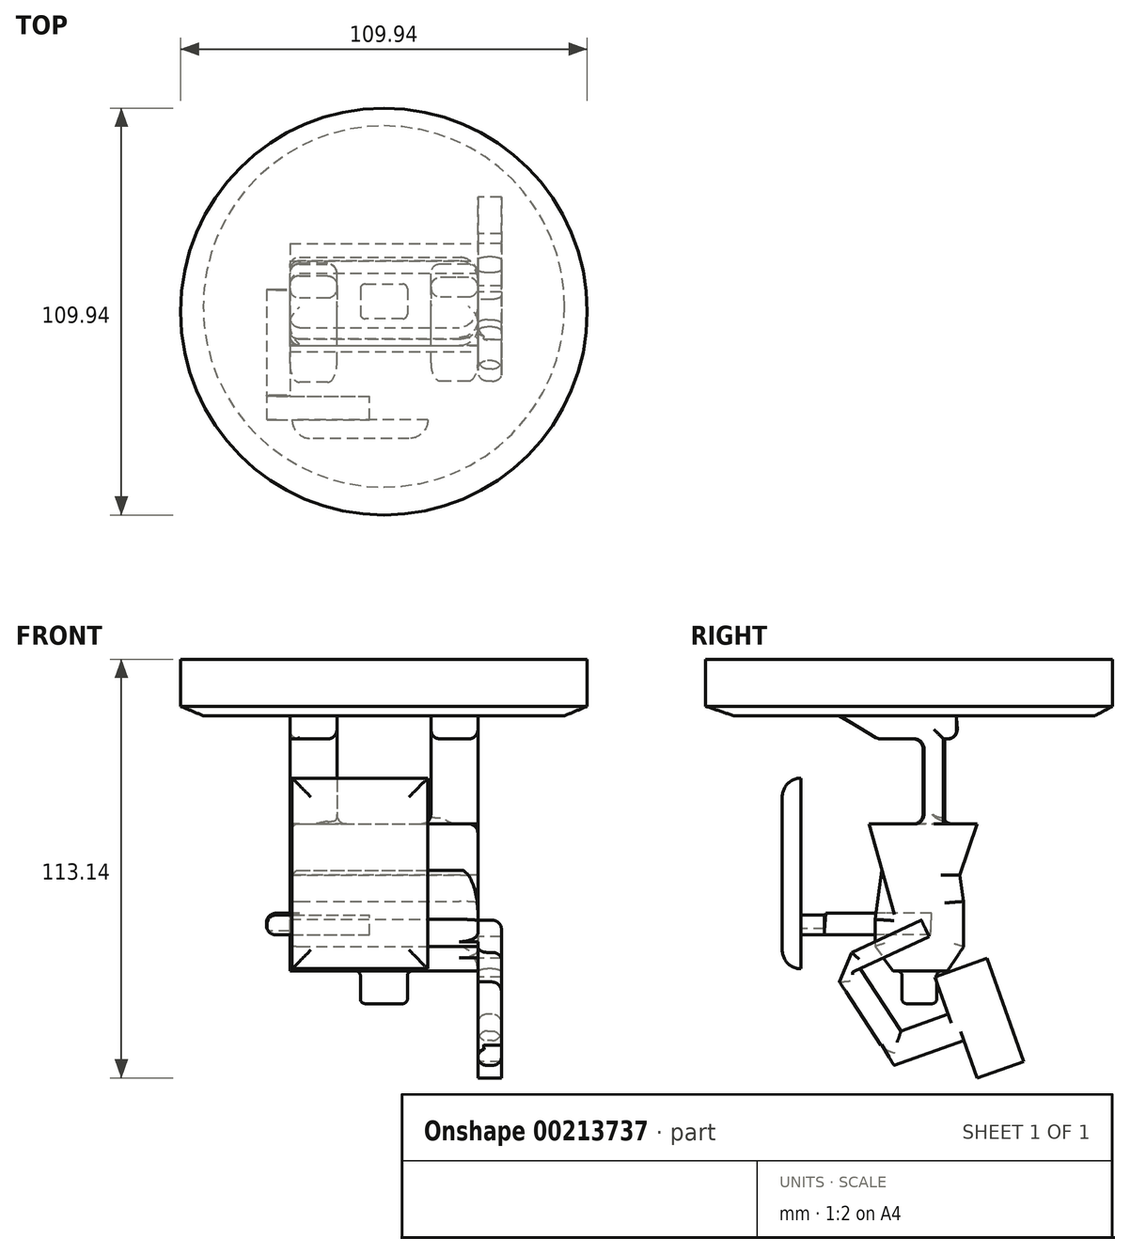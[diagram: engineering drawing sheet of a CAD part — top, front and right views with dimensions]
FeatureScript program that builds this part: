
annotation { "Feature Type Name" : "Feature", "Feature Type Description" : "" }
export const myFeature = defineFeature(function(context is Context, id is Id, definition is map)
    precondition{}
    {
        {
            var Q0;
            Q0=qCreatedBy(makeId("Top.planeOp"),FACE);
            var sketch = newSketch(context, id + "F0", { "sketchPlane" : qUnion([Q0])});
            skCircle(sketch, "E0", {"center": v(0, 0) * mm, "radius": 54.97 * mm});
            skSolve(sketch);
        }
        {
            var Q0;
            Q0 = qSketchRegion(id + "F0", true);
            var Q1;
            Q1=sQuery(id+"F0.wireOp",EDGE,"E0");
            extrude(context, id + "F1", {"entities" : qUnion([Q0]), "surfaceEntities" : qUnion([Q1]), "depth" : 12.7 * mm});
        }
        {
            var Q0;
            Q0=qCreatedBy(makeId("Top.planeOp"),FACE);
            cPlane(context, id + "F2", {"entities" : qUnion([Q0]), "cplaneType" : CPlaneType.OFFSET, "offset" : 2.54 * mm, "oppositeDirection" : true, "width" : 152.4 * mm, "height" : 152.4 * mm});
        }
        {
            var Q0;
            Q0=qCreatedBy(id+"F2.planeOp",FACE);
            var sketch = newSketch(context, id + "F3", { "sketchPlane" : qUnion([Q0])});
            skCircle(sketch, "E1", {"center": v(0, 1.38) * mm, "radius": 48.83 * mm});
            skSolve(sketch);
        }
        {
            var Q0;
            Q0 = qSketchRegion(id + "F3", true);
            var Q1;
            Q1 = qSketchRegion(id + "F0", true);
            loft(context, id + "F4", {"sheetProfilesArray" : [{ "sheetProfileEntities" : qUnion([Q0]) }, { "sheetProfileEntities" : qUnion([Q1]) }]});
        }
        {
            var Q0;
            Q0=qCreatedBy(makeId("Right.planeOp"),FACE);
            cPlane(context, id + "F5", {"entities" : qUnion([Q0]), "cplaneType" : CPlaneType.OFFSET, "offset" : 25.4 * mm, "width" : 152.4 * mm, "height" : 152.4 * mm});
        }
        {
            var Q0;
            Q0=qCreatedBy(makeId("Right.planeOp"),FACE);
            cPlane(context, id + "F6", {"entities" : qUnion([Q0]), "cplaneType" : CPlaneType.OFFSET, "offset" : 25.4 * mm, "oppositeDirection" : true, "width" : 152.4 * mm, "height" : 152.4 * mm});
        }
        {
            var Q0;
            Q0=qCreatedBy(id+"F6.planeOp",FACE);
            var sketch = newSketch(context, id + "F7", { "sketchPlane" : qUnion([Q0])});
            skLineSegment(sketch, "E2", {"start": v(-19.43, -2.33) * mm, "end": v(-8.14, -8.84) * mm});
            skLineSegment(sketch, "E3", {"start": v(-8.14, -8.84) * mm, "end": v(0, -8.84) * mm});
            skLineSegment(sketch, "E4", {"start": v(0, -8.84) * mm, "end": v(6.5, -8.84) * mm});
            skLineSegment(sketch, "E5", {"start": v(6.5, -8.84) * mm, "end": v(13.13, -8.84) * mm});
            skLineSegment(sketch, "E6", {"start": v(13.13, -8.84) * mm, "end": v(12.81, -2.19) * mm});
            skLineSegment(sketch, "E7", {"start": v(12.81, -2.19) * mm, "end": v(-19.43, -2.33) * mm});
            skSolve(sketch);
        }
        {
            var Q0;
            Q0 = qSketchRegion(id + "F7", true);
            extrude(context, id + "F8", {"entities" : qUnion([Q0]), "operationType" : NewBodyOperationType.ADD, "depth" : 12.7 * mm});
        }
        {
            var Q0;
            Q0=qCreatedBy(id+"F5.planeOp",FACE);
            var sketch = newSketch(context, id + "F9", { "sketchPlane" : qUnion([Q0])});
            skLineSegment(sketch, "E8", {"start": v(-19.1, -2.33) * mm, "end": v(-8.3, -8.84) * mm});
            skLineSegment(sketch, "E9", {"start": v(-8.3, -8.84) * mm, "end": v(12.85, -8.84) * mm});
            skLineSegment(sketch, "E10", {"start": v(12.85, -8.84) * mm, "end": v(12.85, -2.33) * mm});
            skLineSegment(sketch, "E11", {"start": v(12.85, -2.33) * mm, "end": v(-19.1, -2.33) * mm});
            skSolve(sketch);
        }
        {
            var Q0;
            Q0 = qSketchRegion(id + "F9", true);
            extrude(context, id + "F10", {"entities" : qUnion([Q0]), "operationType" : NewBodyOperationType.ADD, "oppositeDirection" : true, "depth" : 12.7 * mm});
        }
        {
            var Q0;
            Q0=qCreatedBy(id+"F6.planeOp",FACE);
            var sketch = newSketch(context, id + "F11", { "sketchPlane" : qUnion([Q0])});
            skLineSegment(sketch, "E12", {"start": v(9.67, -8.53) * mm, "end": v(9.67, -32.5) * mm});
            skLineSegment(sketch, "E13", {"start": v(3.73, -8.4) * mm, "end": v(3.73, -32.5) * mm});
            skLineSegment(sketch, "E14", {"start": v(3.73, -32.5) * mm, "end": v(9.67, -32.5) * mm});
            skLineSegment(sketch, "E15", {"start": v(9.67, -8.53) * mm, "end": v(3.73, -8.4) * mm});
            skSolve(sketch);
        }
        {
            var Q0;
            Q0 = qSketchRegion(id + "F11", true);
            extrude(context, id + "F12", {"entities" : qUnion([Q0]), "operationType" : NewBodyOperationType.ADD, "depth" : 12.7 * mm});
        }
        {
            var Q0;
            Q0=qCreatedBy(id+"F5.planeOp",FACE);
            var sketch = newSketch(context, id + "F13", { "sketchPlane" : qUnion([Q0])});
            skLineSegment(sketch, "E16", {"start": v(9.26, -8.56) * mm, "end": v(9.26, -33.06) * mm});
            skLineSegment(sketch, "E17", {"start": v(9.26, -33.06) * mm, "end": v(4, -33.06) * mm});
            skLineSegment(sketch, "E18", {"start": v(4, -33.06) * mm, "end": v(4, -8.28) * mm});
            skLineSegment(sketch, "E19", {"start": v(4, -8.28) * mm, "end": v(9.26, -8.56) * mm});
            skSolve(sketch);
        }
        {
            var Q0;
            Q0 = qSketchRegion(id + "F13", true);
            extrude(context, id + "F14", {"entities" : qUnion([Q0]), "operationType" : NewBodyOperationType.ADD, "oppositeDirection" : true, "depth" : 12.7 * mm});
        }
        {
            var Q0;
            Q0=qCreatedBy(id+"F5.planeOp",FACE);
            var sketch = newSketch(context, id + "F15", { "sketchPlane" : qUnion([Q0])});
            skLineSegment(sketch, "E20", {"start": v(18.38, -31.78) * mm, "end": v(-10.78, -31.78) * mm});
            skLineSegment(sketch, "E21", {"start": v(18.38, -31.78) * mm, "end": v(13.7, -45.64) * mm});
            skLineSegment(sketch, "E22", {"start": v(13.7, -45.64) * mm, "end": v(-6.89, -45.64) * mm});
            skLineSegment(sketch, "E23", {"start": v(-6.89, -45.64) * mm, "end": v(-10.78, -31.78) * mm});
            skSolve(sketch);
        }
        {
            var Q0;
            Q0 = qSketchRegion(id + "F15", true);
            extrude(context, id + "F16", {"entities" : qUnion([Q0]), "operationType" : NewBodyOperationType.ADD, "oppositeDirection" : true, "depth" : 50.8 * mm});
        }
        {
            var Q0;
            Q0=qCreatedBy(id+"F5.planeOp",FACE);
            var sketch = newSketch(context, id + "F17", { "sketchPlane" : qUnion([Q0])});
            skLineSegment(sketch, "E24", {"start": v(-7.36, -44.33) * mm, "end": v(-9.23, -57.6) * mm});
            skLineSegment(sketch, "E25", {"start": v(-9.23, -57.18) * mm, "end": v(-9.23, -64.92) * mm});
            skLineSegment(sketch, "E26", {"start": v(-9.23, -64.92) * mm, "end": v(-4.32, -71.55) * mm});
            skLineSegment(sketch, "E27", {"start": v(-4.32, -71.55) * mm, "end": v(10.33, -71.55) * mm});
            skLineSegment(sketch, "E28", {"start": v(10.33, -71.55) * mm, "end": v(14.75, -64.92) * mm});
            skLineSegment(sketch, "E29", {"start": v(14.75, -64.92) * mm, "end": v(14.75, -52.76) * mm});
            skLineSegment(sketch, "E30", {"start": v(14.75, -52.76) * mm, "end": v(13.5, -44.33) * mm});
            skLineSegment(sketch, "E31", {"start": v(13.5, -44.33) * mm, "end": v(-7.36, -44.33) * mm});
            skSolve(sketch);
        }
        {
            var Q0;
            Q0 = qSketchRegion(id + "F17", true);
            extrude(context, id + "F18", {"entities" : qUnion([Q0]), "operationType" : NewBodyOperationType.ADD, "oppositeDirection" : true, "depth" : 50.8 * mm});
        }
        {
            var Q0;
            Q0=qCreatedBy(makeId("Right.planeOp"),FACE);
            cPlane(context, id + "F19", {"entities" : qUnion([Q0]), "cplaneType" : CPlaneType.OFFSET, "offset" : 6.35 * mm, "width" : 152.4 * mm, "height" : 152.4 * mm});
        }
        {
            var Q0;
            Q0=qCreatedBy(id+"F19.planeOp",FACE);
            var sketch = newSketch(context, id + "F20", { "sketchPlane" : qUnion([Q0])});
            skLineSegment(sketch, "E32.bottom", {"start": v(7.46, -70) * mm, "end": v(-1.93, -70) * mm});
            skLineSegment(sketch, "E32.top", {"start": v(7.46, -80.38) * mm, "end": v(-1.93, -80.38) * mm});
            skLineSegment(sketch, "E32.left", {"start": v(7.46, -70) * mm, "end": v(7.46, -80.38) * mm});
            skLineSegment(sketch, "E32.right", {"start": v(-1.93, -70) * mm, "end": v(-1.93, -80.38) * mm});
            skSolve(sketch);
        }
        {
            var Q0;
            Q0 = qSketchRegion(id + "F20", true);
            extrude(context, id + "F21", {"entities" : qUnion([Q0]), "operationType" : NewBodyOperationType.ADD, "oppositeDirection" : true, "depth" : 12.7 * mm});
        }
        {
            var Q0;
            Q0=makeQuery(id+"F10.opExtrude","SWEPT_EDGE",EDGE,{"disambiguationData":[OSD([sQuery(id+"F9.wireOp",EDGE,"E8"),sQuery(id+"F9.wireOp",EDGE,"E11")])]});
            var Q1;
            Q1=makeQuery(id+"F10.opExtrude","SWEPT_EDGE",EDGE,{"disambiguationData":[OSD([sQuery(id+"F9.wireOp",EDGE,"E8"),sQuery(id+"F9.wireOp",EDGE,"E9")])]});
            var Q2;
            Q2=makeQuery(id+"F8.opExtrude","SWEPT_EDGE",EDGE,{"disambiguationData":[OSD([sQuery(id+"F7.wireOp",EDGE,"E2"),sQuery(id+"F7.wireOp",EDGE,"E3")])]});
            var Q3;
            Q3=makeQuery(id+"F8.opExtrude","SWEPT_EDGE",EDGE,{"disambiguationData":[OSD([sQuery(id+"F7.wireOp",EDGE,"E2"),sQuery(id+"F7.wireOp",EDGE,"E7")])]});
            var Q4;
            Q4=makeQuery(id+"F10.opExtrude","CAP_EDGE",EDGE,{"disambiguationData":[OSD([sQuery(id+"F9.wireOp",EDGE,"E9")])],"isStart":true});
            var Q5;
            Q5=makeQuery(id+"F10.opExtrude","CAP_EDGE",EDGE,{"disambiguationData":[OSD([sQuery(id+"F9.wireOp",EDGE,"E9")])],"isStart":false});
            var Q6;
            Q6=makeQuery(id+"F10.opExtrude","CAP_EDGE",EDGE,{"disambiguationData":[OSD([sQuery(id+"F9.wireOp",EDGE,"E8")])],"isStart":false});
            var Q7;
            Q7=makeQuery(id+"F10.opExtrude","CAP_EDGE",EDGE,{"disambiguationData":[OSD([sQuery(id+"F9.wireOp",EDGE,"E8")])],"isStart":true});
            var Q8;
            Q8=makeQuery(id+"F10.opExtrude","SWEPT_EDGE",EDGE,{"disambiguationData":[OSD([sQuery(id+"F9.wireOp",EDGE,"E9"),sQuery(id+"F9.wireOp",EDGE,"E10")])]});
            var Q9;
            Q9=makeQuery(id+"F10.opExtrude","CAP_EDGE",EDGE,{"disambiguationData":[OSD([sQuery(id+"F9.wireOp",EDGE,"E10")])],"isStart":true});
            var Q10;
            Q10=makeQuery(id+"F10.opExtrude","CAP_EDGE",EDGE,{"disambiguationData":[OSD([sQuery(id+"F9.wireOp",EDGE,"E10")])],"isStart":false});
            var Q11;
            Q11=makeQuery(id+"F8.opExtrude","CAP_EDGE",EDGE,{"disambiguationData":[OSD([sQuery(id+"F7.wireOp",EDGE,"E2")])],"isStart":false});
            var Q12;
            Q12=makeQuery(id+"F8.opExtrude","CAP_EDGE",EDGE,{"disambiguationData":[OSD([sQuery(id+"F7.wireOp",EDGE,"E2")])],"isStart":true});
            var Q13;
            {var subQ0=sQuery(id+"F7.wireOp",EDGE,"E5");var subQ1=sQuery(id+"F7.wireOp",EDGE,"E4");var subQ2=sQuery(id+"F7.wireOp",EDGE,"E3");var subQ4=sQuery(id+"F7.wireOp",EDGE,"E2");Q13=makeQuery(id+"F12.boolean.opBoolean","SPLIT",EDGE,{"disambiguationData":[TD([makeQuery(id+"F8.opExtrude","SWEPT_FACE",FACE,{"disambiguationData":[OSD([subQ4])]})])],"derivedFrom":makeQuery(id+"F8.opExtrude","CAP_EDGE",EDGE,{"disambiguationData":[OSD([subQ2,subQ1,subQ0])],"isStart":false})});}
            var Q14;
            Q14=makeQuery(id+"F14.opExtrude","SWEPT_FACE",FACE,{"disambiguationData":[OSD([sQuery(id+"F13.wireOp",EDGE,"E18")])]});
            var Q15;
            Q15=makeQuery(id+"F12.opExtrude","SWEPT_FACE",FACE,{"disambiguationData":[OSD([sQuery(id+"F11.wireOp",EDGE,"E13")])]});
            fillet(context, id + "F22", {"entities" : qUnion([Q0, Q1, Q2, Q3, Q4, Q5, Q6, Q7, Q8, Q9, Q10, Q11, Q12, Q13, Q14, Q15]), "radius" : 2.54 * mm, "tangentPropagation" : true, "allowEdgeOverflow" : false});
        }
        {
            var Q0;
            Q0=makeQuery(id+"F8.opExtrude","CAP_EDGE",EDGE,{"disambiguationData":[OSD([sQuery(id+"F7.wireOp",EDGE,"E6")])],"isStart":true});
            var Q1;
            Q1=makeQuery(id+"F8.opExtrude","CAP_EDGE",EDGE,{"disambiguationData":[OSD([sQuery(id+"F7.wireOp",EDGE,"E6")])],"isStart":false});
            var Q2;
            Q2=makeQuery(id+"F8.opExtrude","SWEPT_EDGE",EDGE,{"disambiguationData":[OSD([sQuery(id+"F7.wireOp",EDGE,"E5"),sQuery(id+"F7.wireOp",EDGE,"E6")])]});
            var Q3;
            {var subQ0=sQuery(id+"F7.wireOp",EDGE,"E6");var subQ1=sQuery(id+"F7.wireOp",EDGE,"E5");var subQ2=sQuery(id+"F7.wireOp",EDGE,"E4");var subQ3=sQuery(id+"F7.wireOp",EDGE,"E3");Q3=makeQuery(id+"F12.boolean.opBoolean","SPLIT",EDGE,{"disambiguationData":[TD([makeQuery(id+"F8.opExtrude","SWEPT_FACE",FACE,{"disambiguationData":[OSD([subQ0])]})])],"derivedFrom":makeQuery(id+"F8.opExtrude","CAP_EDGE",EDGE,{"disambiguationData":[OSD([subQ3,subQ2,subQ1])],"isStart":false})});}
            var Q4;
            {var subQ1=sQuery(id+"F7.wireOp",EDGE,"E6");var subQ2=sQuery(id+"F7.wireOp",EDGE,"E5");var subQ3=sQuery(id+"F7.wireOp",EDGE,"E4");var subQ4=sQuery(id+"F7.wireOp",EDGE,"E3");Q4=makeQuery(id+"F12.boolean.opBoolean","SPLIT",EDGE,{"disambiguationData":[TD([makeQuery(id+"F8.opExtrude","SWEPT_FACE",FACE,{"disambiguationData":[OSD([subQ1])]})])],"derivedFrom":makeQuery(id+"F8.opExtrude","CAP_EDGE",EDGE,{"disambiguationData":[OSD([subQ4,subQ3,subQ2])],"isStart":true})});}
            fillet(context, id + "F23", {"entities" : qUnion([Q0, Q1, Q2, Q3, Q4]), "radius" : 2.54 * mm, "tangentPropagation" : true, "allowEdgeOverflow" : false});
        }
        {
            var Q0;
            Q0=qCreatedBy(id+"F5.planeOp",FACE);
            var sketch = newSketch(context, id + "F24", { "sketchPlane" : qUnion([Q0])});
            skLineSegment(sketch, "E33", {"start": v(5.37, -62.23) * mm, "end": v(-13.24, -70.87) * mm});
            skLineSegment(sketch, "E34", {"start": v(5.37, -62.23) * mm, "end": v(3.32, -57.8) * mm});
            skLineSegment(sketch, "E35", {"start": v(3.32, -57.8) * mm, "end": v(-15.49, -66.53) * mm});
            skLineSegment(sketch, "E36", {"start": v(-13.24, -70.87) * mm, "end": v(-15.49, -66.53) * mm});
            skLineSegment(sketch, "E37", {"start": v(-15.49, -66.53) * mm, "end": v(-18.8, -74.51) * mm});
            skLineSegment(sketch, "E38", {"start": v(-18.8, -74.51) * mm, "end": v(-13.24, -70.87) * mm});
            skLineSegment(sketch, "E39", {"start": v(-18.8, -74.51) * mm, "end": v(-7.61, -91.59) * mm});
            skLineSegment(sketch, "E40", {"start": v(-13.24, -70.87) * mm, "end": v(-0.95, -89.62) * mm});
            skLineSegment(sketch, "E41", {"start": v(-7.61, -91.59) * mm, "end": v(-0.95, -89.62) * mm});
            skSolve(sketch);
        }
        {
            var Q0;
            Q0 = qSketchRegion(id + "F24", true);
            extrude(context, id + "F25", {"entities" : qUnion([Q0]), "operationType" : NewBodyOperationType.ADD, "depth" : 6.35 * mm});
        }
        {
            var Q0;
            Q0=qCreatedBy(id+"F5.planeOp",FACE);
            var sketch = newSketch(context, id + "F26", { "sketchPlane" : qUnion([Q0])});
            skLineSegment(sketch, "E42", {"start": v(-8.37, -89.92) * mm, "end": v(10.54, -83.2) * mm});
            skLineSegment(sketch, "E43", {"start": v(10.54, -83.2) * mm, "end": v(6.96, -73.13) * mm});
            skLineSegment(sketch, "E44", {"start": v(6.96, -73.13) * mm, "end": v(14.83, -70.34) * mm});
            skLineSegment(sketch, "E45", {"start": v(14.83, -70.34) * mm, "end": v(21.02, -68.14) * mm});
            skLineSegment(sketch, "E46", {"start": v(21.02, -68.14) * mm, "end": v(30.9, -96) * mm});
            skLineSegment(sketch, "E47", {"start": v(30.9, -96) * mm, "end": v(18.41, -100.44) * mm});
            skLineSegment(sketch, "E48", {"start": v(18.41, -100.44) * mm, "end": v(14.83, -90.36) * mm});
            skLineSegment(sketch, "E49", {"start": v(14.83, -90.36) * mm, "end": v(-4.08, -97.07) * mm});
            skLineSegment(sketch, "E50", {"start": v(-4.08, -97.07) * mm, "end": v(-8.37, -89.92) * mm});
            skSolve(sketch);
        }
        {
            var Q0;
            Q0 = qSketchRegion(id + "F26", true);
            extrude(context, id + "F27", {"entities" : qUnion([Q0]), "operationType" : NewBodyOperationType.ADD, "depth" : 6.35 * mm});
        }
        {
            var Q0;
            Q0=qCreatedBy(id+"F6.planeOp",FACE);
            var sketch = newSketch(context, id + "F28", { "sketchPlane" : qUnion([Q0])});
            skLineSegment(sketch, "E51", {"start": v(5.84, -61.79) * mm, "end": v(-22.94, -61.79) * mm});
            skLineSegment(sketch, "E52", {"start": v(6.06, -55.94) * mm, "end": v(-22.5, -55.94) * mm});
            skLineSegment(sketch, "E53", {"start": v(5.84, -61.79) * mm, "end": v(6.06, -55.94) * mm});
            skLineSegment(sketch, "E54", {"start": v(-22.94, -61.79) * mm, "end": v(-22.5, -55.94) * mm});
            skSolve(sketch);
        }
        {
            var Q0;
            Q0 = qSketchRegion(id + "F28", true);
            extrude(context, id + "F29", {"entities" : qUnion([Q0]), "operationType" : NewBodyOperationType.ADD, "oppositeDirection" : true, "depth" : 6.35 * mm});
        }
        {
            var Q0;
            Q0=qCreatedBy(makeId("Front.planeOp"),FACE);
            cPlane(context, id + "F30", {"entities" : qUnion([Q0]), "cplaneType" : CPlaneType.OFFSET, "offset" : 22.86 * mm, "width" : 152.4 * mm, "height" : 152.4 * mm});
        }
        {
            var Q0;
            Q0=qCreatedBy(id+"F30.planeOp",FACE);
            var sketch = newSketch(context, id + "F31", { "sketchPlane" : qUnion([Q0])});
            skLineSegment(sketch, "E55", {"start": v(-31.59, -56.38) * mm, "end": v(-3.88, -56.38) * mm});
            skLineSegment(sketch, "E56", {"start": v(-31.59, -56.38) * mm, "end": v(-31.59, -61.79) * mm});
            skLineSegment(sketch, "E57", {"start": v(-31.59, -61.79) * mm, "end": v(-3.88, -61.79) * mm});
            skLineSegment(sketch, "E58", {"start": v(-3.88, -61.79) * mm, "end": v(-3.88, -56.38) * mm});
            skSolve(sketch);
        }
        {
            var Q0;
            Q0 = qSketchRegion(id + "F31", true);
            extrude(context, id + "F32", {"entities" : qUnion([Q0]), "operationType" : NewBodyOperationType.ADD, "depth" : 6.35 * mm});
        }
        {
            var Q0;
            Q0=qCreatedBy(id+"F30.planeOp",FACE);
            cPlane(context, id + "F33", {"entities" : qUnion([Q0]), "cplaneType" : CPlaneType.OFFSET, "offset" : 6.35 * mm, "width" : 152.4 * mm, "height" : 152.4 * mm});
        }
        {
            var Q0;
            Q0=qCreatedBy(id+"F33.planeOp",FACE);
            var sketch = newSketch(context, id + "F34", { "sketchPlane" : qUnion([Q0])});
            skLineSegment(sketch, "E59.bottom", {"start": v(11.88, -70.96) * mm, "end": v(-24.82, -70.96) * mm});
            skLineSegment(sketch, "E59.top", {"start": v(11.88, -19.4) * mm, "end": v(-24.82, -19.4) * mm});
            skLineSegment(sketch, "E59.left", {"start": v(11.88, -70.96) * mm, "end": v(11.88, -19.4) * mm});
            skLineSegment(sketch, "E59.right", {"start": v(-24.82, -70.96) * mm, "end": v(-24.82, -19.4) * mm});
            skSolve(sketch);
        }
        {
            var Q0;
            Q0 = qSketchRegion(id + "F34", true);
            extrude(context, id + "F35", {"entities" : qUnion([Q0]), "operationType" : NewBodyOperationType.ADD, "depth" : 5.08 * mm});
        }
        {
            var Q0;
            Q0=makeQuery(id+"F35.opExtrude","CAP_EDGE",EDGE,{"disambiguationData":[OSD([sQuery(id+"F34.wireOp",EDGE,"E59.left")])],"isStart":false});
            var Q1;
            Q1=makeQuery(id+"F35.opExtrude","CAP_EDGE",EDGE,{"disambiguationData":[OSD([sQuery(id+"F34.wireOp",EDGE,"E59.bottom")])],"isStart":false});
            var Q2;
            Q2=makeQuery(id+"F35.opExtrude","CAP_EDGE",EDGE,{"disambiguationData":[OSD([sQuery(id+"F34.wireOp",EDGE,"E59.top")])],"isStart":false});
            var Q3;
            Q3=makeQuery(id+"F35.opExtrude","CAP_EDGE",EDGE,{"disambiguationData":[OSD([sQuery(id+"F34.wireOp",EDGE,"E59.right")])],"isStart":false});
            fillet(context, id + "F36", {"entities" : qUnion([Q0, Q1, Q2, Q3]), "radius" : 5.08 * mm, "tangentPropagation" : true, "allowEdgeOverflow" : false});
        }
        {
            var Q0;
            Q0=makeQuery(id+"F14.opExtrude","CAP_EDGE",EDGE,{"disambiguationData":[OSD([sQuery(id+"F13.wireOp",EDGE,"E16")])],"isStart":true});
            var Q1;
            Q1=makeQuery(id+"F14.opExtrude","CAP_EDGE",EDGE,{"disambiguationData":[OSD([sQuery(id+"F13.wireOp",EDGE,"E16")])],"isStart":false});
            var Q2;
            Q2=makeQuery(id+"F12.opExtrude","CAP_EDGE",EDGE,{"disambiguationData":[OSD([sQuery(id+"F11.wireOp",EDGE,"E12")])],"isStart":false});
            var Q3;
            Q3=makeQuery(id+"F12.opExtrude","CAP_EDGE",EDGE,{"disambiguationData":[OSD([sQuery(id+"F11.wireOp",EDGE,"E12")])],"isStart":true});
            fillet(context, id + "F37", {"entities" : qUnion([Q0, Q1, Q2, Q3]), "radius" : 2.54 * mm, "tangentPropagation" : true, "allowEdgeOverflow" : false});
        }
        {
            var Q0;
            Q0=makeQuery(id+"F18.opExtrude","CAP_EDGE",EDGE,{"disambiguationData":[OSD([sQuery(id+"F17.wireOp",EDGE,"E29")])],"isStart":true});
            var Q1;
            Q1=makeQuery(id+"F18.opExtrude","CAP_EDGE",EDGE,{"disambiguationData":[OSD([sQuery(id+"F17.wireOp",EDGE,"E30")])],"isStart":true});
            var Q2;
            Q2=makeQuery(id+"F18.opExtrude","CAP_EDGE",EDGE,{"disambiguationData":[OSD([sQuery(id+"F17.wireOp",EDGE,"E24")])],"isStart":true});
            var Q3;
            {var subQ0=sQuery(id+"F17.wireOp",EDGE,"E24");var subQ2=sQuery(id+"F17.wireOp",EDGE,"E25");Q3=makeQuery(id+"F25.boolean.opBoolean","SPLIT",EDGE,{"disambiguationData":[TD([makeQuery(id+"F18.opExtrude","SWEPT_FACE",FACE,{"disambiguationData":[OSD([subQ0])]})])],"derivedFrom":makeQuery(id+"F18.opExtrude","CAP_EDGE",EDGE,{"disambiguationData":[OSD([subQ2])],"isStart":true})});}
            var Q4;
            {var subQ0=sQuery(id+"F17.wireOp",EDGE,"E26");var subQ1=sQuery(id+"F17.wireOp",EDGE,"E27");Q4=makeQuery(id+"F25.boolean.opBoolean","SPLIT",EDGE,{"disambiguationData":[TD([makeQuery(id+"F18.opExtrude","SWEPT_FACE",FACE,{"disambiguationData":[OSD([subQ1])]})])],"derivedFrom":makeQuery(id+"F18.opExtrude","CAP_EDGE",EDGE,{"disambiguationData":[OSD([subQ0])],"isStart":true})});}
            fillet(context, id + "F38", {"entities" : qUnion([Q0, Q1, Q2, Q3, Q4]), "radius" : 5.08 * mm, "tangentPropagation" : true, "allowEdgeOverflow" : false});
        }
        {
            var Q0;
            Q0=makeQuery(id+"F18.opExtrude","CAP_EDGE",EDGE,{"disambiguationData":[OSD([sQuery(id+"F17.wireOp",EDGE,"E26")])],"isStart":false});
            var Q1;
            {var subQ0=sQuery(id+"F17.wireOp",EDGE,"E26");var subQ1=sQuery(id+"F17.wireOp",EDGE,"E25");Q1=makeQuery(id+"F29.boolean.opBoolean","SPLIT",EDGE,{"disambiguationData":[TD([makeQuery(id+"F18.opExtrude","SWEPT_FACE",FACE,{"disambiguationData":[OSD([subQ0])]})])],"derivedFrom":makeQuery(id+"F18.opExtrude","CAP_EDGE",EDGE,{"disambiguationData":[OSD([subQ1])],"isStart":false})});}
            var Q2;
            {var subQ0=sQuery(id+"F17.wireOp",EDGE,"E24");var subQ2=sQuery(id+"F17.wireOp",EDGE,"E31");Q2=makeQuery(id+"F29.boolean.opBoolean","SPLIT",EDGE,{"disambiguationData":[TD([makeQuery(id+"F18.opExtrude","SWEPT_FACE",FACE,{"disambiguationData":[OSD([subQ2])]})])],"derivedFrom":makeQuery(id+"F18.opExtrude","CAP_EDGE",EDGE,{"disambiguationData":[OSD([subQ0])],"isStart":false})});}
            var Q3;
            Q3=makeQuery(id+"F18.opExtrude","CAP_EDGE",EDGE,{"disambiguationData":[OSD([sQuery(id+"F17.wireOp",EDGE,"E28")])],"isStart":false});
            var Q4;
            Q4=makeQuery(id+"F18.opExtrude","CAP_EDGE",EDGE,{"disambiguationData":[OSD([sQuery(id+"F17.wireOp",EDGE,"E29")])],"isStart":false});
            var Q5;
            Q5=makeQuery(id+"F18.opExtrude","CAP_EDGE",EDGE,{"disambiguationData":[OSD([sQuery(id+"F17.wireOp",EDGE,"E30")])],"isStart":false});
            var Q6;
            Q6=makeQuery(id+"F27.opExtrude","CAP_EDGE",EDGE,{"disambiguationData":[OSD([sQuery(id+"F26.wireOp",EDGE,"E49")])],"isStart":true});
            var Q7;
            Q7=makeQuery(id+"F27.opExtrude","CAP_EDGE",EDGE,{"disambiguationData":[OSD([sQuery(id+"F26.wireOp",EDGE,"E42")])],"isStart":true});
            fillet(context, id + "F39", {"entities" : qUnion([Q0, Q1, Q2, Q3, Q4, Q5, Q6, Q7]), "radius" : 2.54 * mm, "tangentPropagation" : true, "allowEdgeOverflow" : false});
        }
        {
            var Q0;
            Q0=makeQuery(id+"F29.opExtrude","CAP_EDGE",EDGE,{"disambiguationData":[OSD([sQuery(id+"F28.wireOp",EDGE,"E51")])],"isStart":false});
            var Q1;
            Q1=makeQuery(id+"F29.opExtrude","CAP_EDGE",EDGE,{"disambiguationData":[OSD([sQuery(id+"F28.wireOp",EDGE,"E52")])],"isStart":false});
            var Q2;
            Q2=makeQuery(id+"F32.opExtrude","SWEPT_EDGE",EDGE,{"disambiguationData":[OSD([sQuery(id+"F31.wireOp",EDGE,"E55"),sQuery(id+"F31.wireOp",EDGE,"E56")])]});
            fillet(context, id + "F40", {"entities" : qUnion([Q0, Q1, Q2]), "radius" : 2.54 * mm, "tangentPropagation" : true, "allowEdgeOverflow" : false});
        }
        {
            var Q0;
            Q0=makeQuery(id+"F25.opExtrude","CAP_EDGE",EDGE,{"disambiguationData":[OSD([sQuery(id+"F24.wireOp",EDGE,"E35")])],"isStart":false});
            var Q1;
            Q1=makeQuery(id+"F25.opExtrude","CAP_EDGE",EDGE,{"disambiguationData":[OSD([sQuery(id+"F24.wireOp",EDGE,"E37")])],"isStart":false});
            var Q2;
            Q2=makeQuery(id+"F27.opExtrude","CAP_EDGE",EDGE,{"disambiguationData":[OSD([sQuery(id+"F26.wireOp",EDGE,"E49")])],"isStart":false});
            var Q3;
            Q3=makeQuery(id+"F27.opExtrude","CAP_EDGE",EDGE,{"disambiguationData":[OSD([sQuery(id+"F26.wireOp",EDGE,"E42")])],"isStart":false});
            var Q4;
            Q4=makeQuery(id+"F25.opExtrude","CAP_EDGE",EDGE,{"disambiguationData":[OSD([sQuery(id+"F24.wireOp",EDGE,"E40")])],"isStart":false});
            fillet(context, id + "F41", {"entities" : qUnion([Q0, Q1, Q2, Q3, Q4]), "radius" : 2.54 * mm, "tangentPropagation" : true, "allowEdgeOverflow" : false});
        }
        {
            var Q0;
            Q0=makeQuery(id+"F25.opExtrude","CAP_EDGE",EDGE,{"disambiguationData":[OSD([sQuery(id+"F24.wireOp",EDGE,"E37")])],"isStart":true});
            var Q1;
            Q1=makeQuery(id+"F25.opExtrude","CAP_EDGE",EDGE,{"disambiguationData":[OSD([sQuery(id+"F24.wireOp",EDGE,"E39")])],"isStart":true});
            var Q2;
            Q2=makeQuery(id+"F25.opExtrude","CAP_EDGE",EDGE,{"disambiguationData":[OSD([sQuery(id+"F24.wireOp",EDGE,"E40")])],"isStart":true});
            var Q3;
            {var subQ0=sQuery(id+"F26.wireOp",EDGE,"E42");Q3=makeQuery(id+"F41.opFillet","BLEND_EDGE",EDGE,{"blendedFrom":[makeQuery(id+"F27.opExtrude","CAP_EDGE",EDGE,{"disambiguationData":[OSD([subQ0])],"isStart":false}),makeQuery(id+"F27.boolean.opBoolean","MERGE",FACE,{"derivedFrom":[makeQuery(id+"F25.opExtrude","CAP_FACE",FACE,{"disambiguationData":[OSD([sQuery(id+"F24.wireOp",EDGE,"E33"),sQuery(id+"F24.wireOp",EDGE,"E34"),sQuery(id+"F24.wireOp",EDGE,"E35"),sQuery(id+"F24.wireOp",EDGE,"E37"),sQuery(id+"F24.wireOp",EDGE,"E39"),sQuery(id+"F24.wireOp",EDGE,"E40"),sQuery(id+"F24.wireOp",EDGE,"E41")])],"isStart":false}),makeQuery(id+"F27.opExtrude","CAP_FACE",FACE,{"disambiguationData":[OSD([subQ0,sQuery(id+"F26.wireOp",EDGE,"E43"),sQuery(id+"F26.wireOp",EDGE,"E44"),sQuery(id+"F26.wireOp",EDGE,"E45"),sQuery(id+"F26.wireOp",EDGE,"E46"),sQuery(id+"F26.wireOp",EDGE,"E47"),sQuery(id+"F26.wireOp",EDGE,"E48"),sQuery(id+"F26.wireOp",EDGE,"E49"),sQuery(id+"F26.wireOp",EDGE,"E50")])],"isStart":false})]})],"blendedInto":[makeQuery(id+"F27.boolean.opBoolean","MERGE",FACE,{"derivedFrom":[makeQuery(id+"F25.opExtrude","CAP_FACE",FACE,{"disambiguationData":[OSD([sQuery(id+"F24.wireOp",EDGE,"E33"),sQuery(id+"F24.wireOp",EDGE,"E34"),sQuery(id+"F24.wireOp",EDGE,"E35"),sQuery(id+"F24.wireOp",EDGE,"E37"),sQuery(id+"F24.wireOp",EDGE,"E39"),sQuery(id+"F24.wireOp",EDGE,"E40"),sQuery(id+"F24.wireOp",EDGE,"E41")])],"isStart":false}),makeQuery(id+"F27.opExtrude","CAP_FACE",FACE,{"disambiguationData":[OSD([subQ0,sQuery(id+"F26.wireOp",EDGE,"E43"),sQuery(id+"F26.wireOp",EDGE,"E44"),sQuery(id+"F26.wireOp",EDGE,"E45"),sQuery(id+"F26.wireOp",EDGE,"E46"),sQuery(id+"F26.wireOp",EDGE,"E47"),sQuery(id+"F26.wireOp",EDGE,"E48"),sQuery(id+"F26.wireOp",EDGE,"E49"),sQuery(id+"F26.wireOp",EDGE,"E50")])],"isStart":false})]})]});}
            var Q4;
            {var subQ0=sQuery(id+"F26.wireOp",EDGE,"E42");Q4=makeQuery(id+"F41.opFillet","BLEND_EDGE",EDGE,{"blendedFrom":[makeQuery(id+"F27.opExtrude","CAP_EDGE",EDGE,{"disambiguationData":[OSD([subQ0])],"isStart":false}),makeQuery(id+"F27.opExtrude","SWEPT_FACE",FACE,{"disambiguationData":[OSD([subQ0])]})],"blendedInto":[makeQuery(id+"F27.opExtrude","SWEPT_FACE",FACE,{"disambiguationData":[OSD([subQ0])]})]});}
            fillet(context, id + "F42", {"entities" : qUnion([Q0, Q1, Q2, Q3, Q4]), "radius" : 2.54 * mm, "tangentPropagation" : true, "allowEdgeOverflow" : false});
        }
        {
            var Q0;
            Q0=makeQuery(id+"F21.opExtrude","SWEPT_EDGE",EDGE,{"disambiguationData":[OSD([sQuery(id+"F20.wireOp",EDGE,"E32.top"),sQuery(id+"F20.wireOp",EDGE,"E32.right")])]});
            var Q1;
            Q1=makeQuery(id+"F21.opExtrude","CAP_EDGE",EDGE,{"disambiguationData":[OSD([sQuery(id+"F20.wireOp",EDGE,"E32.top")])],"isStart":true});
            var Q2;
            Q2=makeQuery(id+"F21.opExtrude","SWEPT_EDGE",EDGE,{"disambiguationData":[OSD([sQuery(id+"F20.wireOp",EDGE,"E32.top"),sQuery(id+"F20.wireOp",EDGE,"E32.left")])]});
            var Q3;
            Q3=makeQuery(id+"F21.opExtrude","CAP_EDGE",EDGE,{"disambiguationData":[OSD([sQuery(id+"F20.wireOp",EDGE,"E32.top")])],"isStart":false});
            var Q4;
            Q4=makeQuery(id+"F21.boolean.opBoolean","INTERSECT",EDGE,{"derivedFrom":[makeQuery(id+"F18.opExtrude","SWEPT_FACE",FACE,{"disambiguationData":[OSD([sQuery(id+"F17.wireOp",EDGE,"E27")])]}),makeQuery(id+"F21.opExtrude","SWEPT_FACE",FACE,{"disambiguationData":[OSD([sQuery(id+"F20.wireOp",EDGE,"E32.right")])]})]});
            var Q5;
            Q5=makeQuery(id+"F21.boolean.opBoolean","INTERSECT",EDGE,{"derivedFrom":[makeQuery(id+"F18.opExtrude","SWEPT_FACE",FACE,{"disambiguationData":[OSD([sQuery(id+"F17.wireOp",EDGE,"E27")])]}),makeQuery(id+"F21.opExtrude","CAP_FACE",FACE,{"disambiguationData":[OSD([sQuery(id+"F20.wireOp",EDGE,"E32.bottom"),sQuery(id+"F20.wireOp",EDGE,"E32.top"),sQuery(id+"F20.wireOp",EDGE,"E32.left"),sQuery(id+"F20.wireOp",EDGE,"E32.right")])],"isStart":false})]});
            var Q6;
            Q6=makeQuery(id+"F21.opExtrude","CAP_EDGE",EDGE,{"disambiguationData":[OSD([sQuery(id+"F20.wireOp",EDGE,"E32.right")])],"isStart":false});
            var Q7;
            Q7=makeQuery(id+"F21.opExtrude","CAP_EDGE",EDGE,{"disambiguationData":[OSD([sQuery(id+"F20.wireOp",EDGE,"E32.right")])],"isStart":true});
            var Q8;
            Q8=makeQuery(id+"F21.opExtrude","CAP_EDGE",EDGE,{"disambiguationData":[OSD([sQuery(id+"F20.wireOp",EDGE,"E32.left")])],"isStart":true});
            var Q9;
            Q9=makeQuery(id+"F21.boolean.opBoolean","INTERSECT",EDGE,{"derivedFrom":[makeQuery(id+"F18.opExtrude","SWEPT_FACE",FACE,{"disambiguationData":[OSD([sQuery(id+"F17.wireOp",EDGE,"E27")])]}),makeQuery(id+"F21.opExtrude","SWEPT_FACE",FACE,{"disambiguationData":[OSD([sQuery(id+"F20.wireOp",EDGE,"E32.left")])]})]});
            var Q10;
            Q10=makeQuery(id+"F21.opExtrude","CAP_EDGE",EDGE,{"disambiguationData":[OSD([sQuery(id+"F20.wireOp",EDGE,"E32.left")])],"isStart":false});
            var Q11;
            Q11=makeQuery(id+"F21.boolean.opBoolean","INTERSECT",EDGE,{"derivedFrom":[makeQuery(id+"F18.opExtrude","SWEPT_FACE",FACE,{"disambiguationData":[OSD([sQuery(id+"F17.wireOp",EDGE,"E27")])]}),makeQuery(id+"F21.opExtrude","CAP_FACE",FACE,{"disambiguationData":[OSD([sQuery(id+"F20.wireOp",EDGE,"E32.bottom"),sQuery(id+"F20.wireOp",EDGE,"E32.top"),sQuery(id+"F20.wireOp",EDGE,"E32.left"),sQuery(id+"F20.wireOp",EDGE,"E32.right")])],"isStart":true})]});
            fillet(context, id + "F43", {"entities" : qUnion([Q0, Q1, Q2, Q3, Q4, Q5, Q6, Q7, Q8, Q9, Q10, Q11]), "radius" : 1.27 * mm, "tangentPropagation" : true, "allowEdgeOverflow" : false});
        }
    });
